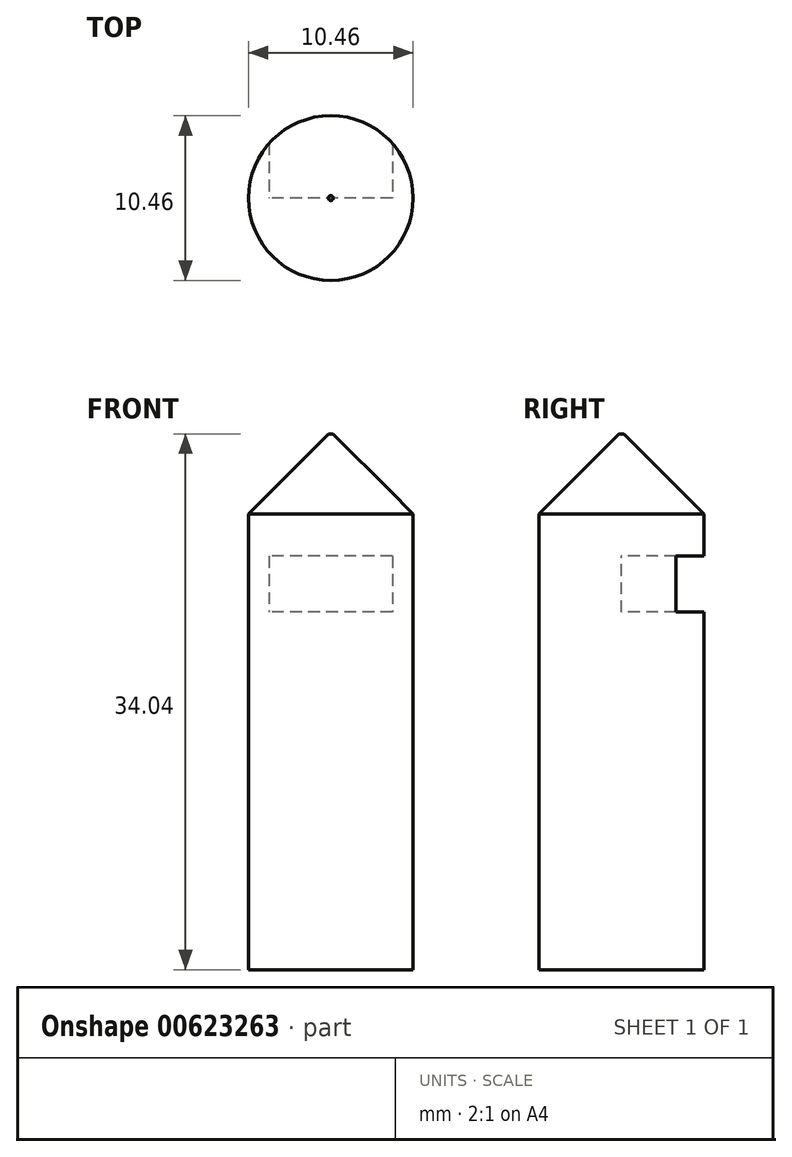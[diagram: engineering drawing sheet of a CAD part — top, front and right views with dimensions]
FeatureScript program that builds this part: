
annotation { "Feature Type Name" : "Feature", "Feature Type Description" : "" }
export const myFeature = defineFeature(function(context is Context, id is Id, definition is map)
    precondition{}
    {
        {
            var Q0;
            Q0=qCreatedBy(makeId("Top.planeOp"),FACE);
            var sketch = newSketch(context, id + "F0", { "sketchPlane" : qUnion([Q0])});
            skCircle(sketch, "E0", {"center": v(0, 0) * mm, "radius": 5.23 * mm});
            skSolve(sketch);
        }
        {
            var Q0;
            Q0 = qSketchRegion(id + "F0", true);
            extrude(context, id + "F1", {"entities" : qUnion([Q0]), "depth" : 34.04 * mm, "offsetDistance" : 25.4 * mm});
        }
        {
            var Q0;
            Q0=makeQuery(id+"F1.opExtrude","CAP_EDGE",EDGE,{"disambiguationData":[OSD([sQuery(id+"F0.wireOp",EDGE,"E0")])],"isStart":false});
            chamfer(context, id + "F2", {"entities" : qUnion([Q0]), "width" : 5.08 * mm, "tangentPropagation" : true});
        }
        {
            var Q0;
            Q0=qCreatedBy(makeId("Front.planeOp"),FACE);
            var sketch = newSketch(context, id + "F3", { "sketchPlane" : qUnion([Q0])});
            skLineSegment(sketch, "E1.bottom", {"start": v(3.91, 22.71) * mm, "end": v(-3.91, 22.71) * mm});
            skLineSegment(sketch, "E1.top", {"start": v(3.91, 26.28) * mm, "end": v(-3.91, 26.28) * mm});
            skLineSegment(sketch, "E1.left", {"start": v(3.91, 22.71) * mm, "end": v(3.91, 26.28) * mm});
            skLineSegment(sketch, "E1.right", {"start": v(-3.91, 22.71) * mm, "end": v(-3.91, 26.28) * mm});
            skPoint(sketch, "E1.middle", {"position": v(0, 24.5) * mm});
            skSolve(sketch);
        }
        {
            var Q0;
            Q0 = qSketchRegion(id + "F3", true);
            extrude(context, id + "F4", {"entities" : qUnion([Q0]), "operationType" : NewBodyOperationType.REMOVE, "oppositeDirection" : true, "depth" : 25.4 * mm, "offsetDistance" : 25.4 * mm});
        }
    });
